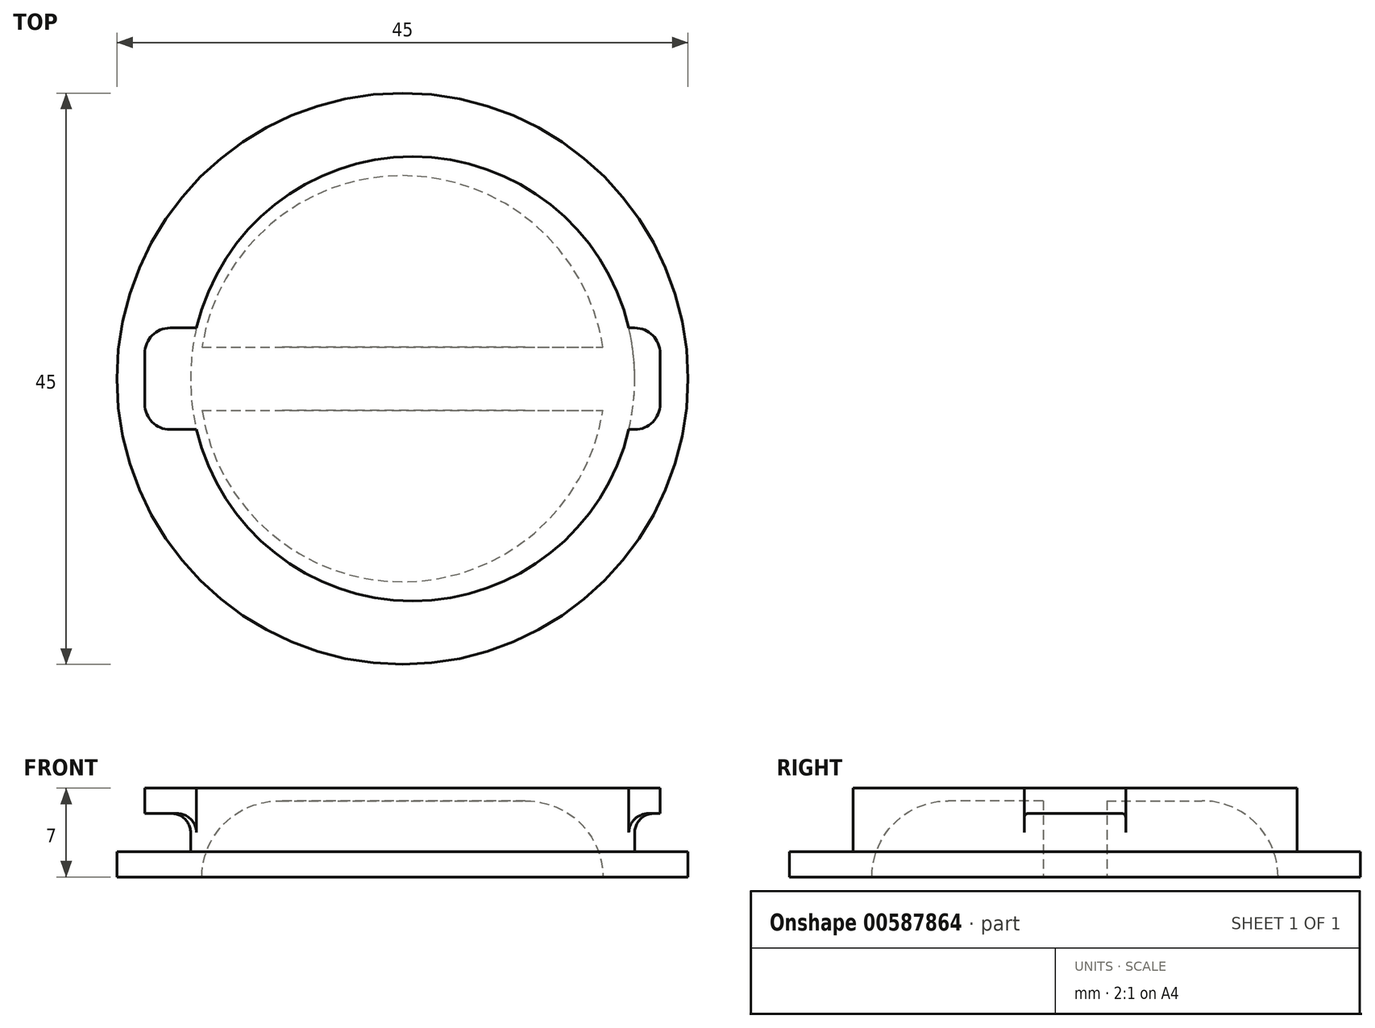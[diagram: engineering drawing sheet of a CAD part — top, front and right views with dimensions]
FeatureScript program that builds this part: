
annotation { "Feature Type Name" : "Feature", "Feature Type Description" : "" }
export const myFeature = defineFeature(function(context is Context, id is Id, definition is map)
    precondition{}
    {
        {
            var Q0;
            Q0=qCreatedBy(makeId("Top.planeOp"),FACE);
            var sketch = newSketch(context, id + "F0", { "sketchPlane" : qUnion([Q0])});
            skCircle(sketch, "E0", {"center": v(0, 0) * mm, "radius": 22.5 * mm});
            skSolve(sketch);
        }
        {
            var Q0;
            Q0=makeQuery(id+"F0.imprint","IMPRINT",FACE,{"disambiguationData":[TD([[makeQuery(id+"F0.imprint","IMPRINT",EDGE,{"derivedFrom":sQuery(id+"F0.wireOp",EDGE,"E0")}),1.0]])]});
            extrude(context, id + "F1", {"entities" : qUnion([Q0]), "depth" : 2 * mm, "offsetDistance" : 25 * mm});
        }
        {
            var Q0;
            Q0=makeQuery(id+"F1.opExtrude","CAP_FACE",FACE,{"disambiguationData":[OSD([sQuery(id+"F0.wireOp",EDGE,"E0")])],"isStart":false});
            var sketch = newSketch(context, id + "F2", { "sketchPlane" : qUnion([Q0])});
            skCircle(sketch, "E1", {"center": v(0.8, 0) * mm, "radius": 17.5 * mm});
            skSolve(sketch);
        }
        {
            var Q0;
            Q0=makeQuery(id+"F2.imprint","IMPRINT",FACE,{"disambiguationData":[TD([[makeQuery(id+"F2.imprint","IMPRINT",EDGE,{"derivedFrom":sQuery(id+"F2.wireOp",EDGE,"E1")}),1.0]])]});
            extrude(context, id + "F3", {"entities" : qUnion([Q0]), "operationType" : NewBodyOperationType.ADD, "depth" : 5 * mm, "offsetDistance" : 25 * mm});
        }
        {
            var Q0;
            Q0=makeQuery(id+"F3.opExtrude","CAP_FACE",FACE,{"disambiguationData":[OSD([sQuery(id+"F2.wireOp",EDGE,"E1")])],"isStart":false});
            var sketch = newSketch(context, id + "F4", { "sketchPlane" : qUnion([Q0])});
            skLineSegment(sketch, "E2.bottom", {"start": v(20.3, -4) * mm, "end": v(-20.3, -4) * mm});
            skLineSegment(sketch, "E2.top", {"start": v(20.3, 4) * mm, "end": v(-20.3, 4) * mm});
            skLineSegment(sketch, "E2.left", {"start": v(20.3, -4) * mm, "end": v(20.3, 4) * mm});
            skLineSegment(sketch, "E2.right", {"start": v(-20.3, -4) * mm, "end": v(-20.3, 4) * mm});
            skPoint(sketch, "E2.middle", {"position": v(0, 0) * mm});
            skSolve(sketch);
        }
        {
            var Q0;
            {var subQ0=sQuery(id+"F4.wireOp",EDGE,"E2.right");Q0=makeQuery(id+"F4.imprint","IMPRINT",FACE,{"disambiguationData":[TD([[makeQuery(id+"F4.imprint","IMPRINT",EDGE,{"derivedFrom":subQ0}),-1.0]])]});}
            var Q1;
            {var subQ0=sQuery(id+"F4.wireOp",EDGE,"E2.bottom");var subQ1=makeQuery(id+"F3.opExtrude","CAP_EDGE",EDGE,{"disambiguationData":[OSD([sQuery(id+"F2.wireOp",EDGE,"E1")])],"isStart":false});var subQ2=makeQuery(id+"F4.imprint","INTERSECT",VERTEX,{"disambiguationData":[OD(0.0)],"derivedFrom":[subQ1,subQ0]});Q1=makeQuery(id+"F4.imprint","IMPRINT",FACE,{"disambiguationData":[TD([[makeQuery(id+"F4.imprint","IMPRINT",EDGE,{"disambiguationData":[TD([[subQ2,-1.0]])],"derivedFrom":subQ0}),-1.0]])]});}
            var Q2;
            {var subQ0=sQuery(id+"F4.wireOp",EDGE,"E2.left");Q2=makeQuery(id+"F4.imprint","IMPRINT",FACE,{"disambiguationData":[TD([[makeQuery(id+"F4.imprint","IMPRINT",EDGE,{"derivedFrom":subQ0}),1.0]])]});}
            extrude(context, id + "F5", {"entities" : qUnion([Q0, Q1, Q2]), "operationType" : NewBodyOperationType.ADD, "oppositeDirection" : true, "depth" : 2 * mm, "offsetDistance" : 25 * mm});
        }
        {
            var Q0;
            Q0=makeQuery(id+"F5.boolean.opBoolean","INTERSECT",EDGE,{"disambiguationData":[OD(0.0)],"derivedFrom":[makeQuery(id+"F3.opExtrude","SWEPT_FACE",FACE,{"disambiguationData":[OSD([sQuery(id+"F2.wireOp",EDGE,"E1")])]}),makeQuery(id+"F5.opExtrude","CAP_FACE",FACE,{"disambiguationData":[OSD([sQuery(id+"F4.wireOp",EDGE,"E2.bottom"),sQuery(id+"F4.wireOp",EDGE,"E2.top"),sQuery(id+"F4.wireOp",EDGE,"E2.left"),sQuery(id+"F4.wireOp",EDGE,"E2.right")])],"isStart":false})]});
            var Q1;
            Q1=makeQuery(id+"F5.boolean.opBoolean","INTERSECT",EDGE,{"disambiguationData":[OD(1.0)],"derivedFrom":[makeQuery(id+"F3.opExtrude","SWEPT_FACE",FACE,{"disambiguationData":[OSD([sQuery(id+"F2.wireOp",EDGE,"E1")])]}),makeQuery(id+"F5.opExtrude","CAP_FACE",FACE,{"disambiguationData":[OSD([sQuery(id+"F4.wireOp",EDGE,"E2.bottom"),sQuery(id+"F4.wireOp",EDGE,"E2.top"),sQuery(id+"F4.wireOp",EDGE,"E2.left"),sQuery(id+"F4.wireOp",EDGE,"E2.right")])],"isStart":false})]});
            fillet(context, id + "F6", {"entities" : qUnion([Q0, Q1]), "radius" : 1.5 * mm, "tangentPropagation" : true, "allowEdgeOverflow" : false});
        }
        {
            var Q0;
            Q0=makeQuery(id+"F5.opExtrude","SWEPT_EDGE",EDGE,{"disambiguationData":[OSD([sQuery(id+"F4.wireOp",EDGE,"E2.top"),sQuery(id+"F4.wireOp",EDGE,"E2.right")])]});
            var Q1;
            Q1=makeQuery(id+"F5.opExtrude","SWEPT_EDGE",EDGE,{"disambiguationData":[OSD([sQuery(id+"F4.wireOp",EDGE,"E2.bottom"),sQuery(id+"F4.wireOp",EDGE,"E2.right")])]});
            var Q2;
            Q2=makeQuery(id+"F5.opExtrude","SWEPT_EDGE",EDGE,{"disambiguationData":[OSD([sQuery(id+"F4.wireOp",EDGE,"E2.bottom"),sQuery(id+"F4.wireOp",EDGE,"E2.left")])]});
            var Q3;
            Q3=makeQuery(id+"F5.opExtrude","SWEPT_EDGE",EDGE,{"disambiguationData":[OSD([sQuery(id+"F4.wireOp",EDGE,"E2.top"),sQuery(id+"F4.wireOp",EDGE,"E2.left")])]});
            fillet(context, id + "F7", {"entities" : qUnion([Q0, Q1, Q2, Q3]), "radius" : 2 * mm, "tangentPropagation" : true, "allowEdgeOverflow" : false});
        }
        {
            var Q0;
            Q0=makeQuery(id+"F1.opExtrude","CAP_FACE",FACE,{"disambiguationData":[OSD([sQuery(id+"F0.wireOp",EDGE,"E0")])],"isStart":true});
            var sketch = newSketch(context, id + "F8", { "sketchPlane" : qUnion([Q0])});
            skCircle(sketch, "E3", {"center": v(0, 0) * mm, "radius": 16 * mm});
            skSolve(sketch);
        }
        {
            var Q0;
            Q0=makeQuery(id+"F8.imprint","IMPRINT",FACE,{"disambiguationData":[TD([[makeQuery(id+"F8.imprint","IMPRINT",EDGE,{"derivedFrom":sQuery(id+"F8.wireOp",EDGE,"E3")}),1.0]])]});
            extrude(context, id + "F9", {"entities" : qUnion([Q0]), "operationType" : NewBodyOperationType.REMOVE, "oppositeDirection" : true, "depth" : 6 * mm, "offsetDistance" : 25 * mm});
        }
        {
            var Q0;
            Q0=makeQuery(id+"F9.boolean.opBoolean","COPY",EDGE,{"derivedFrom":makeQuery(id+"F9.opExtrude","CAP_EDGE",EDGE,{"disambiguationData":[OSD([sQuery(id+"F8.wireOp",EDGE,"E3")])],"isStart":false})});
            fillet(context, id + "F10", {"entities" : qUnion([Q0]), "radius" : 6 * mm, "tangentPropagation" : true, "allowEdgeOverflow" : false});
        }
        {
            var Q0;
            Q0=makeQuery(id+"F1.opExtrude","CAP_FACE",FACE,{"disambiguationData":[OSD([sQuery(id+"F0.wireOp",EDGE,"E0")])],"isStart":true});
            var sketch = newSketch(context, id + "F11", { "sketchPlane" : qUnion([Q0])});
            skLineSegment(sketch, "E4.bottom", {"start": v(-22.36, 2.5) * mm, "end": v(22.36, 2.5) * mm});
            skLineSegment(sketch, "E4.top", {"start": v(-22.36, -2.5) * mm, "end": v(22.36, -2.5) * mm});
            skLineSegment(sketch, "E4.left", {"start": v(-22.36, 2.5) * mm, "end": v(-22.36, -2.5) * mm});
            skLineSegment(sketch, "E4.right", {"start": v(22.36, 2.5) * mm, "end": v(22.36, -2.5) * mm});
            skPoint(sketch, "E4.middle", {"position": v(0, 0) * mm});
            skSolve(sketch);
        }
        {
            var Q0;
            {var subQ0=sQuery(id+"F11.wireOp",EDGE,"E4.bottom");var subQ1=makeQuery(id+"F10.opFillet","BLEND_EDGE",EDGE,{"blendedFrom":[makeQuery(id+"F9.boolean.opBoolean","COPY",EDGE,{"derivedFrom":makeQuery(id+"F9.opExtrude","CAP_EDGE",EDGE,{"disambiguationData":[OSD([sQuery(id+"F8.wireOp",EDGE,"E3")])],"isStart":false})}),makeQuery(id+"F1.opExtrude","CAP_FACE",FACE,{"disambiguationData":[OSD([sQuery(id+"F0.wireOp",EDGE,"E0")])],"isStart":true})],"blendedInto":[makeQuery(id+"F1.opExtrude","CAP_FACE",FACE,{"disambiguationData":[OSD([sQuery(id+"F0.wireOp",EDGE,"E0")])],"isStart":true})]});var subQ2=makeQuery(id+"F11.imprint","INTERSECT",VERTEX,{"disambiguationData":[OD(0.0)],"derivedFrom":[subQ1,subQ0]});Q0=makeQuery(id+"F11.imprint","IMPRINT",FACE,{"disambiguationData":[TD([[makeQuery(id+"F11.imprint","IMPRINT",EDGE,{"disambiguationData":[TD([[subQ2,-1.0]])],"derivedFrom":subQ0}),-1.0]])]});}
            extrude(context, id + "F12", {"entities" : qUnion([Q0]), "operationType" : NewBodyOperationType.ADD, "endBound" : BoundingType.UP_TO_NEXT, "oppositeDirection" : true, "depth" : 25 * mm, "offsetDistance" : 25 * mm});
        }
    });
